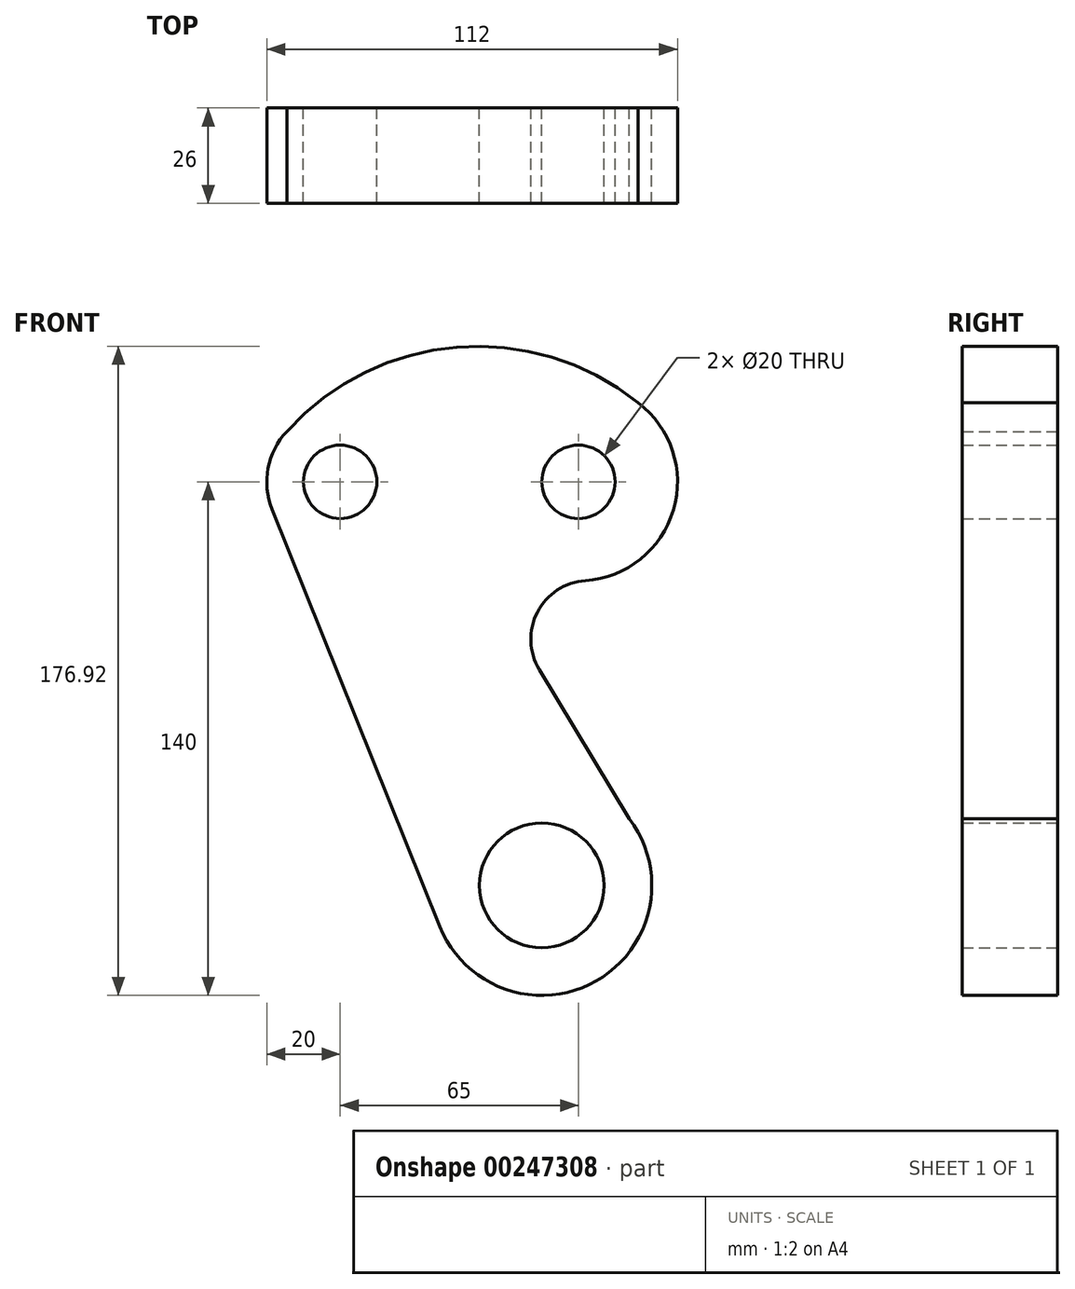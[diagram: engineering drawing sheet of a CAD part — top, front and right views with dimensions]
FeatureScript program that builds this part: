
annotation { "Feature Type Name" : "Feature", "Feature Type Description" : "" }
export const myFeature = defineFeature(function(context is Context, id is Id, definition is map)
    precondition{}
    {
        {
            var Q0;
            Q0=qCreatedBy(makeId("Front.planeOp"),FACE);
            var sketch = newSketch(context, id + "F0", { "sketchPlane" : qUnion([Q0])});
            skArc(sketch, "E0", {"start": v(-27.83, -11.2) * mm, "mid": v(14.8, -26.1) * mm, "end": v(23.89, 18.15) * mm});
            skCircle(sketch, "E1", {"center": v(0, 0) * mm, "radius": 17 * mm});
            skCircle(sketch, "E2", {"center": v(10, 110) * mm, "radius": 10 * mm});
            skCircle(sketch, "E3", {"center": v(-55, 110) * mm, "radius": 10 * mm});
            skArc(sketch, "E4", {"start": v(-37.88, 120.35) * mm, "mid": v(-63.93, 127.9) * mm, "end": v(-73.56, 102.54) * mm});
            skArc(sketch, "E5", {"start": v(11.88, 83.07) * mm, "mid": v(35.88, 102.3) * mm, "end": v(26.3, 131.53) * mm});
            skArc(sketch, "E6", {"start": v(11.88, 83.07) * mm, "mid": v(-1.2, 74.47) * mm, "end": v(-0.7, 58.83) * mm});
            skLineSegment(sketch, "E7", {"start": v(-27.83, -11.2) * mm, "end": v(-73.56, 102.54) * mm});
            skLineSegment(sketch, "E8", {"start": v(-37.88, 120.35) * mm, "end": v(23.89, 18.15) * mm});
            skArc(sketch, "E9.trimOffspring", {"start": v(26.3, 131.53) * mm, "mid": v(-23.18, 146.69) * mm, "end": v(-69.56, 123.71) * mm});
            skLineSegment(sketch, "E10", {"start": v(-96.7, 110) * mm, "end": v(62.07, 110) * mm, "construction": true});
            skLineSegment(sketch, "E11", {"start": v(-55, 144.02) * mm, "end": v(-55, 77.84) * mm, "construction": true});
            skLineSegment(sketch, "E12", {"start": v(10, 145.74) * mm, "end": v(10, 76.12) * mm, "construction": true});
            skLineSegment(sketch, "E13", {"start": v(-42.87, 0) * mm, "end": v(46.3, 0) * mm, "construction": true});
            skLineSegment(sketch, "E14", {"start": v(0, 35.32) * mm, "end": v(0, -41.5) * mm, "construction": true});
            skSolve(sketch);
        }
        {
            var Q0;
            {var subQ4=sQuery(id+"F0.wireOp",EDGE,"E0");Q0=makeQuery(id+"F0.imprint","IMPRINT",FACE,{"disambiguationData":[TD([[makeQuery(id+"F0.imprint","IMPRINT",EDGE,{"derivedFrom":subQ4}),1.0]])]});}
            var Q1;
            Q1=makeQuery(id+"F0.imprint","IMPRINT",FACE,{"disambiguationData":[TD([[makeQuery(id+"F0.imprint","IMPRINT",EDGE,{"derivedFrom":sQuery(id+"F0.wireOp",EDGE,"E2")}),-1.0]])]});
            extrude(context, id + "F1", {"entities" : qUnion([Q0, Q1]), "depth" : 26 * mm});
        }
    });
